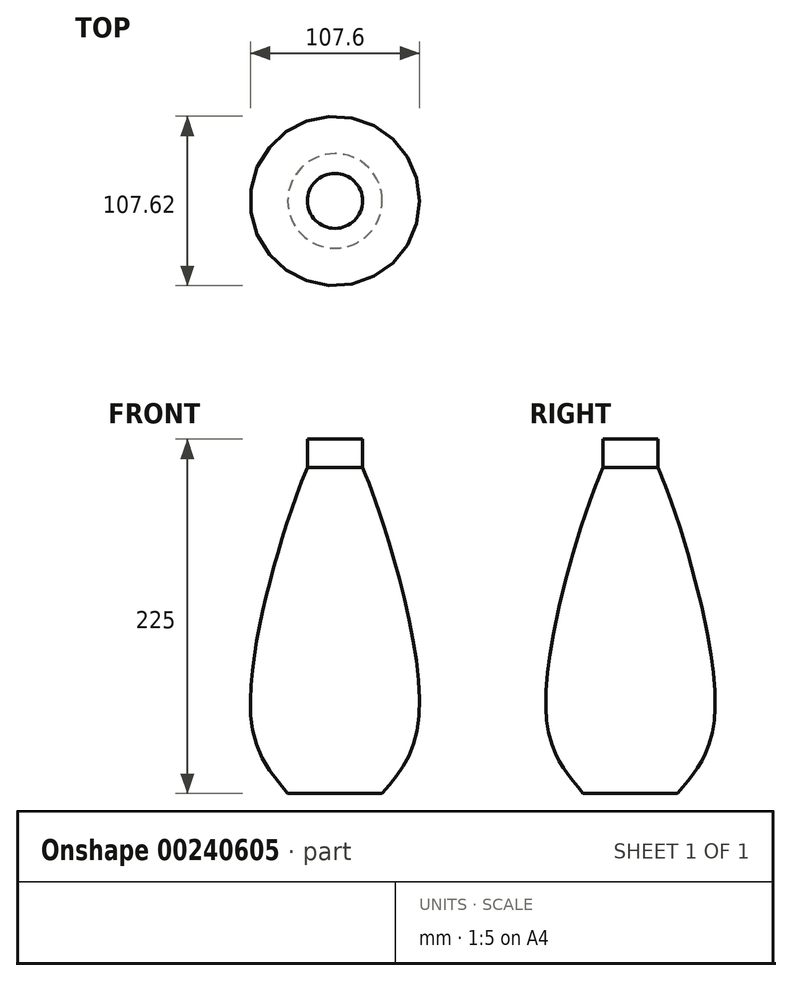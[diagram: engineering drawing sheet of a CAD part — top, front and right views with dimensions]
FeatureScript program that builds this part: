
annotation { "Feature Type Name" : "Feature", "Feature Type Description" : "" }
export const myFeature = defineFeature(function(context is Context, id is Id, definition is map)
    precondition{}
    {
        {
            var Q0;
            Q0=qCreatedBy(makeId("Front.planeOp"),FACE);
            var sketch = newSketch(context, id + "F0", { "sketchPlane" : qUnion([Q0])});
            skLineSegment(sketch, "E0", {"start": v(0, 115.3) * mm, "end": v(0, -109.7) * mm});
            skLineSegment(sketch, "E1", {"start": v(0, -109.7) * mm, "end": v(-30, -109.7) * mm});
            skLineSegment(sketch, "E2", {"start": v(0, 115.3) * mm, "end": v(-17.5, 115.3) * mm});
            skLineSegment(sketch, "E3", {"start": v(-17.5, 115.3) * mm, "end": v(-17.5, 97.24) * mm});
            skFitSpline(sketch, "E4", {"points": [v(-17.5, 97.24) * mm, v(-30.28, 62.69) * mm, v(-53.3, -62.68) * mm, v(-30, -109.7) * mm], "startDerivative": vector(-44.46, -107.51) * mm, "endDerivative": vector(107.11, -125.68) * mm});
            skSolve(sketch);
        }
        {
            var Q0;
            Q0 = qSketchRegion(id + "F0", true);
            var Q1;
            Q1=sQuery(id+"F0.wireOp",EDGE,"E0");
            revolve(context, id + "F1", {"entities" : qUnion([Q0]), "axis" : qUnion([Q1]), "revolveType" : RevolveType.FULL});
        }
    });
